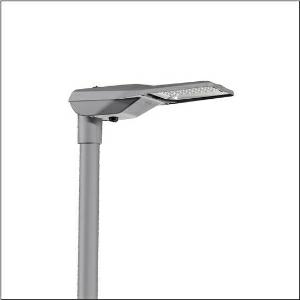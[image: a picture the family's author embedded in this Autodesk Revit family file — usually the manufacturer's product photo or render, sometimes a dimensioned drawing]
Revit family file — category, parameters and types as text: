
# Revit family: streetlight_sl_21_iq_mini___p1_0a_5xe2a31y08gb_f1ed
name_source: partatom
category: Lighting Fixtures
units: mm (PartAtom-declared; Revit-internal decimal feet)

## family parameters
Cut with Voids When Loaded = No
Host = Face
Light Source = No
Part Type = Normal
Room Calculation Point = No
Round Connector Dimension = Use Diameter
Shared = No

## types (1)
- --- (1 x LED, 5990 lm, 39.8 W, 3000K)
    Apparent Load = 40 VA
    CIE Flux Codes = 21 50 90 100 100
    Color Rendering = 70
    Color Temperature = 3000K
    Default Elevation = 1800 mm
    Description = Streetlight SL 21 iQ mini, mast luminaire, primary light control with lens, of PMMA, primary optical cover: cover, of toughened safety glass, transparent, light distribution: P1.0a, light emission: direct distribution, primary light characteristic: asymmetric, installation type: post-top, side-entry, LED, High Power LED, rated luminous flux: 5.990lm, luminous efficacy: 151lm/W, light colour: 730, colour temperature: 3000K, control gear: iQ-Street Remote, D4i with power reduction, control: pre-setting: logarithmic dimming characteristic, Street-Remote, Auto-Match, Temp-Guard, Lumen-Switch, Night-Set, Smart-Wire, Light-Fading, Desk-Remote (wireless, voltage-free reading and setting of iQ features in the workshop via application-optimized NFC function/RFID function), optimised constant luminous flux control (CLO 2.0), mains connection: 220..240V, AC, 50/60Hz, start of lifetime: 40W, end of service life: 41W, reduction: 18W, luminaire housing, of diecast aluminium, powder-coated, Siteco® metallic grey (DB 702S), corrosivity category C5 mid according to DIN EN ISO 12944, please order mast flange separately, inclination adjustable: 0°, 5°, 10°, 15°, sealing non-destructively replaceable, multi-level sealing system, length: 628mm, width: 235mm, height: 110mm, mast flange for spigot size: 42mm (side-entry): 5XC10008XM4, 60/48mm (side-entry/post-top): 5XC10108XM2, 76/60mm (side-entry/post-top): 5XC10108XM1, mounting height: 4..8m, Smart Interface below and above, protection rating (complete): IP66, insulation class (complete): insulation class II (safety insulation), certification: CE, ENEC, ENEC+, VDE, impact resistance: IK10, permissible operating ambient temperature for outdoor applications: -40..+50°C, standard-compliant lighting for roads and squares, packaging unit: 1 piece

Light Distribution: P1.0a
    Height = 110 mm
    Lamp = 1 x LED
    Lamp Light Flux = 5990 lm
    Lamp Power = 39.8 W
    Lamp count = 1
    Length = 625 mm
    Luminous efficacy = 151 lm/W
    Manufacturer = Siteco
    ModVariant = No
    Model = 5XE2A31Y08GB
    Number of Poles = 1
    OnlyDefault = Yes
    Power Factor = 1
    Product Name = Streetlight SL 21 iQ mini | P1.0a
    Product group = mast luminaire | pylon top
    ProductGroupID = 6100
    Protection Class = Protection class II
    Protection Degree = IP 66
    RLX_Detail_Level = 1
    RLX_Emergency_Light_Flux = 0 lm
    RLX_Emergency_Type = 0
    RLX_Emergency_Type_DB = No
    RlxData = <blob elided: 104005 chars, md5=8ddc53e8>
    Socket = socket
    Standby Power = 0 W
    System Light Flux = 5990 lm
    System Power = 40 W
    Type Comments = factory setting: luminous flux: 100 % | dim-lin: 254 | 800 mA
    Type Image = l_1003514.jpg
    URL = http://relux.com
    VarID = @adj_135015
    Voltage = 0 V
    Weight = 0.00 kg
    Width = 234 mm

## geometry (parser evidence)
native form markers: Blend x4, Sweep x10
no freeform markers — native parametric forms only
